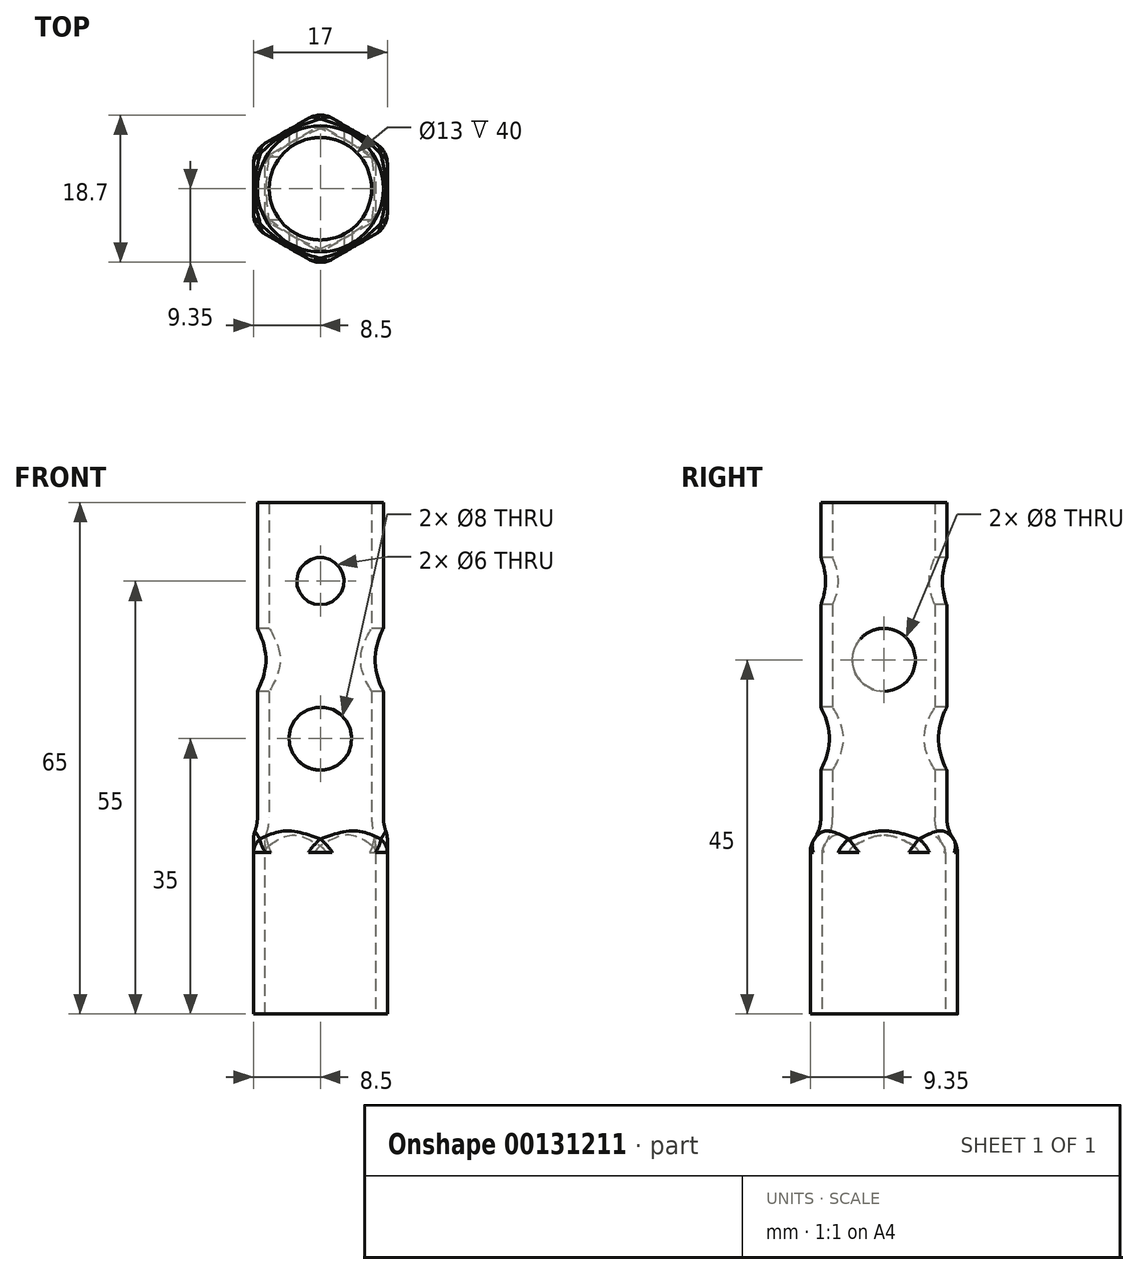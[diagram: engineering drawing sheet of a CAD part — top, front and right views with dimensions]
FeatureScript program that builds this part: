
annotation { "Feature Type Name" : "Feature", "Feature Type Description" : "" }
export const myFeature = defineFeature(function(context is Context, id is Id, definition is map)
    precondition{}
    {
        {
            var Q0;
            Q0=qCreatedBy(makeId("Top.planeOp"),FACE);
            var sketch = newSketch(context, id + "F0", { "sketchPlane" : qUnion([Q0])});
            skCircle(sketch, "E0.cCircle", {"center": v(0, 0) * mm, "radius": 8.5 * mm, "construction": true});
            skLineSegment(sketch, "E0.0", {"start": v(8.5, 4.9) * mm, "end": v(8.5, -4.9) * mm});
            skLineSegment(sketch, "E0.1", {"start": v(8.5, -4.9) * mm, "end": v(0, -9.81) * mm});
            skLineSegment(sketch, "E0.2", {"start": v(0, -9.81) * mm, "end": v(-8.5, -4.9) * mm});
            skLineSegment(sketch, "E0.3", {"start": v(-8.5, -4.9) * mm, "end": v(-8.5, 4.9) * mm});
            skLineSegment(sketch, "E0.4", {"start": v(-8.5, 4.9) * mm, "end": v(0, 9.81) * mm});
            skLineSegment(sketch, "E0.5", {"start": v(0, 9.81) * mm, "end": v(8.5, 4.9) * mm});
            skPoint(sketch, "E0.0.midPoint", {"position": v(8.5, 0) * mm});
            skSolve(sketch);
        }
        {
            var Q0;
            Q0=makeQuery(id+"F0.imprint","IMPRINT",FACE,{"disambiguationData":[TD([[makeQuery(id+"F0.imprint","IMPRINT",EDGE,{"derivedFrom":sQuery(id+"F0.wireOp",EDGE,"E0.0")}),-1.0]])]});
            var Q1;
            Q1=qCreatedBy(id+"FDWVjlBbFMlSgu2_1.planeOp",FACE);
            extrude(context, id + "F1", {"entities" : qUnion([Q0]), "endBoundEntityFace" : qUnion([Q1]), "depth" : 65 * mm});
        }
        {
            var Q0;
            Q0=qCreatedBy(makeId("Top.planeOp"),FACE);
            cPlane(context, id + "F2", {"entities" : qUnion([Q0]), "cplaneType" : CPlaneType.OFFSET, "offset" : 20 * mm, "width" : 150 * mm, "height" : 150 * mm});
        }
        {
            var Q0;
            Q0=qCreatedBy(id+"F2.planeOp",FACE);
            var sketch = newSketch(context, id + "F3", { "sketchPlane" : qUnion([Q0])});
            skCircle(sketch, "E1", {"center": v(0, 0) * mm, "radius": 8 * mm});
            skCircle(sketch, "E2", {"center": v(0, 0) * mm, "radius": 24 * mm});
            skSolve(sketch);
        }
        {
            var Q0;
            Q0=makeQuery(id+"F3.imprint","IMPRINT",FACE,{"disambiguationData":[TD([[makeQuery(id+"F3.imprint","IMPRINT",EDGE,{"derivedFrom":sQuery(id+"F3.wireOp",EDGE,"E1")}),-1.0]])]});
            extrude(context, id + "F4", {"entities" : qUnion([Q0]), "depth" : 100 * mm});
        }
        {
            var Q0;
            Q0=makeQuery(id+"F4.opExtrude","CAP_EDGE",EDGE,{"disambiguationData":[OSD([sQuery(id+"F3.wireOp",EDGE,"E1")])],"isStart":true});
            fillet(context, id + "F5", {"entities" : qUnion([Q0]), "radius" : 5 * mm, "tangentPropagation" : true, "allowEdgeOverflow" : false});
        }
        {
            var Q0;
            Q0=makeQuery(id+"F4.opExtrude","SWEPT_BODY",BODY,{"disambiguationData":[OSD([sQuery(id+"F3.wireOp",EDGE,"E1"),sQuery(id+"F3.wireOp",EDGE,"E2")])]});
            var Q1;
            Q1=makeQuery(id+"F1.opExtrude","SWEPT_BODY",BODY,{"disambiguationData":[OSD([sQuery(id+"F0.wireOp",EDGE,"E0.0"),sQuery(id+"F0.wireOp",EDGE,"E0.1"),sQuery(id+"F0.wireOp",EDGE,"E0.2"),sQuery(id+"F0.wireOp",EDGE,"E0.3"),sQuery(id+"F0.wireOp",EDGE,"E0.4"),sQuery(id+"F0.wireOp",EDGE,"E0.5")])]});
            booleanBodies(context, id + "F6", {"operationType" : BooleanOperationType.SUBTRACTION, "tools" : qUnion([Q0]), "targets" : qUnion([Q1])});
        }
        {
            var Q0;
            Q0=makeQuery(id+"F1.opExtrude","SWEPT_EDGE",EDGE,{"disambiguationData":[OSD([sQuery(id+"F0.wireOp",EDGE,"E0.1"),sQuery(id+"F0.wireOp",EDGE,"E0.2")])]});
            var Q1;
            Q1=makeQuery(id+"F1.opExtrude","SWEPT_EDGE",EDGE,{"disambiguationData":[OSD([sQuery(id+"F0.wireOp",EDGE,"E0.0"),sQuery(id+"F0.wireOp",EDGE,"E0.1")])]});
            var Q2;
            Q2=makeQuery(id+"F1.opExtrude","SWEPT_EDGE",EDGE,{"disambiguationData":[OSD([sQuery(id+"F0.wireOp",EDGE,"E0.0"),sQuery(id+"F0.wireOp",EDGE,"E0.5")])]});
            var Q3;
            Q3=makeQuery(id+"F1.opExtrude","SWEPT_EDGE",EDGE,{"disambiguationData":[OSD([sQuery(id+"F0.wireOp",EDGE,"E0.4"),sQuery(id+"F0.wireOp",EDGE,"E0.5")])]});
            var Q4;
            Q4=makeQuery(id+"F1.opExtrude","SWEPT_EDGE",EDGE,{"disambiguationData":[OSD([sQuery(id+"F0.wireOp",EDGE,"E0.3"),sQuery(id+"F0.wireOp",EDGE,"E0.4")])]});
            var Q5;
            Q5=makeQuery(id+"F1.opExtrude","SWEPT_EDGE",EDGE,{"disambiguationData":[OSD([sQuery(id+"F0.wireOp",EDGE,"E0.2"),sQuery(id+"F0.wireOp",EDGE,"E0.3")])]});
            fillet(context, id + "F7", {"entities" : qUnion([Q0, Q1, Q2, Q3, Q4, Q5]), "radius" : 3 * mm, "tangentPropagation" : true, "allowEdgeOverflow" : false});
        }
        {
            var Q0;
            Q0=makeQuery(id+"F6.opBoolean","INTERSECT",EDGE,{"derivedFrom":[makeQuery(id+"F1.opExtrude","SWEPT_FACE",FACE,{"disambiguationData":[OSD([sQuery(id+"F0.wireOp",EDGE,"E0.0")])]}),makeQuery(id+"F5.opFillet","BLEND_FACE",FACE,{"disambiguationData":[OSD([sQuery(id+"F3.wireOp",EDGE,"E1")])]})]});
            fillet(context, id + "F8", {"entities" : qUnion([Q0]), "radius" : 3 * mm, "tangentPropagation" : true, "allowEdgeOverflow" : false});
        }
        {
            var Q0;
            Q0=makeQuery(id+"F1.opExtrude","CAP_FACE",FACE,{"disambiguationData":[OSD([sQuery(id+"F0.wireOp",EDGE,"E0.0"),sQuery(id+"F0.wireOp",EDGE,"E0.1"),sQuery(id+"F0.wireOp",EDGE,"E0.2"),sQuery(id+"F0.wireOp",EDGE,"E0.3"),sQuery(id+"F0.wireOp",EDGE,"E0.4"),sQuery(id+"F0.wireOp",EDGE,"E0.5")])],"isStart":false});
            var Q1;
            Q1=makeQuery(id+"F1.opExtrude","CAP_FACE",FACE,{"disambiguationData":[OSD([sQuery(id+"F0.wireOp",EDGE,"E0.0"),sQuery(id+"F0.wireOp",EDGE,"E0.1"),sQuery(id+"F0.wireOp",EDGE,"E0.2"),sQuery(id+"F0.wireOp",EDGE,"E0.3"),sQuery(id+"F0.wireOp",EDGE,"E0.4"),sQuery(id+"F0.wireOp",EDGE,"E0.5")])],"isStart":true});
            shell(context, id + "F9", {"entities" : qUnion([Q0, Q1]), "thickness" : 1.5 * mm});
        }
        {
            var Q0;
            Q0=qCreatedBy(makeId("Front.planeOp"),FACE);
            var sketch = newSketch(context, id + "F10", { "sketchPlane" : qUnion([Q0])});
            skCircle(sketch, "E3", {"center": v(0, 55) * mm, "radius": 3 * mm});
            skCircle(sketch, "E4", {"center": v(0, 35) * mm, "radius": 4 * mm});
            skSolve(sketch);
        }
        {
            var Q0;
            Q0 = qSketchRegion(id + "F10", true);
            extrude(context, id + "F11", {"entities" : qUnion([Q0]), "operationType" : NewBodyOperationType.REMOVE, "endBound" : BoundingType.THROUGH_ALL, "oppositeDirection" : true, "depth" : 25 * mm, "hasSecondDirection" : true, "secondDirectionBound" : BoundingType.THROUGH_ALL, "secondDirectionOppositeDirection" : false, "secondDirectionDepth" : 25 * mm});
        }
        {
            var Q0;
            Q0=qCreatedBy(makeId("Right.planeOp"),FACE);
            var sketch = newSketch(context, id + "F12", { "sketchPlane" : qUnion([Q0])});
            skCircle(sketch, "E5", {"center": v(0, 45) * mm, "radius": 4 * mm});
            skSolve(sketch);
        }
        {
            var Q0;
            Q0=makeQuery(id+"F12.imprint","IMPRINT",FACE,{"disambiguationData":[TD([[makeQuery(id+"F12.imprint","IMPRINT",EDGE,{"derivedFrom":sQuery(id+"F12.wireOp",EDGE,"E5")}),1.0]])]});
            extrude(context, id + "F13", {"entities" : qUnion([Q0]), "operationType" : NewBodyOperationType.REMOVE, "endBound" : BoundingType.THROUGH_ALL, "depth" : 25 * mm, "hasSecondDirection" : true, "secondDirectionBound" : BoundingType.THROUGH_ALL, "secondDirectionOppositeDirection" : true, "secondDirectionDepth" : 25 * mm});
        }
    });
